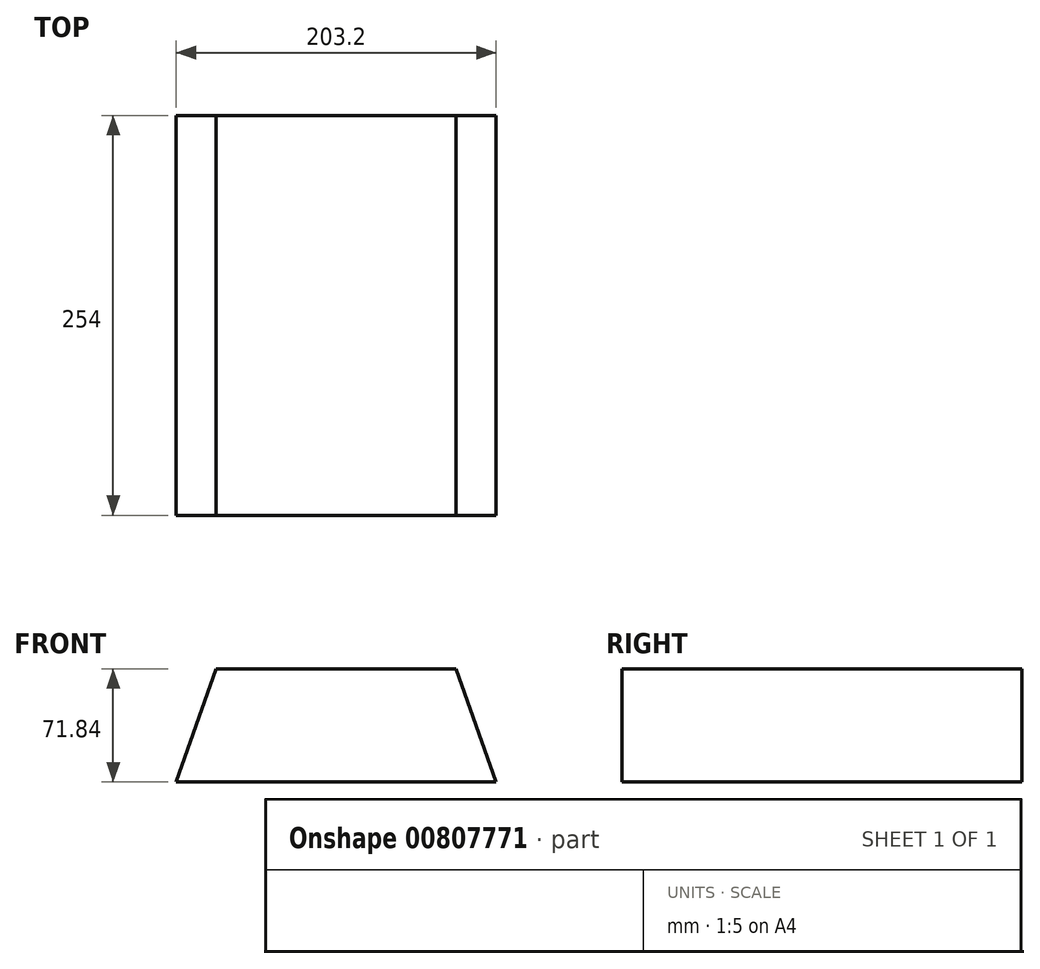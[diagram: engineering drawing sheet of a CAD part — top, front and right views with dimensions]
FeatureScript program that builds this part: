
annotation { "Feature Type Name" : "Feature", "Feature Type Description" : "" }
export const myFeature = defineFeature(function(context is Context, id is Id, definition is map)
    precondition{}
    {
        {
            var Q0;
            Q0=qCreatedBy(makeId("Front.planeOp"),FACE);
            var sketch = newSketch(context, id + "F0", { "sketchPlane" : qUnion([Q0])});
            skLineSegment(sketch, "E0", {"start": v(-79, -71.84) * mm, "end": v(124.2, -71.84) * mm});
            skLineSegment(sketch, "E1", {"start": v(124.2, -71.84) * mm, "end": v(98.8, 0) * mm});
            skLineSegment(sketch, "E2", {"start": v(98.8, 0) * mm, "end": v(-53.6, 0) * mm});
            skLineSegment(sketch, "E3", {"start": v(-79, -71.84) * mm, "end": v(-53.6, 0) * mm});
            skSolve(sketch);
        }
        {
            var Q0;
            Q0=makeQuery(id+"F0.imprint","IMPRINT",FACE,{"disambiguationData":[TD([[makeQuery(id+"F0.imprint","IMPRINT",EDGE,{"derivedFrom":sQuery(id+"F0.wireOp",EDGE,"E0")}),1.0]])]});
            extrude(context, id + "F1", {"entities" : qUnion([Q0]), "depth" : 254 * mm, "offsetDistance" : 25.4 * mm});
        }
    });
